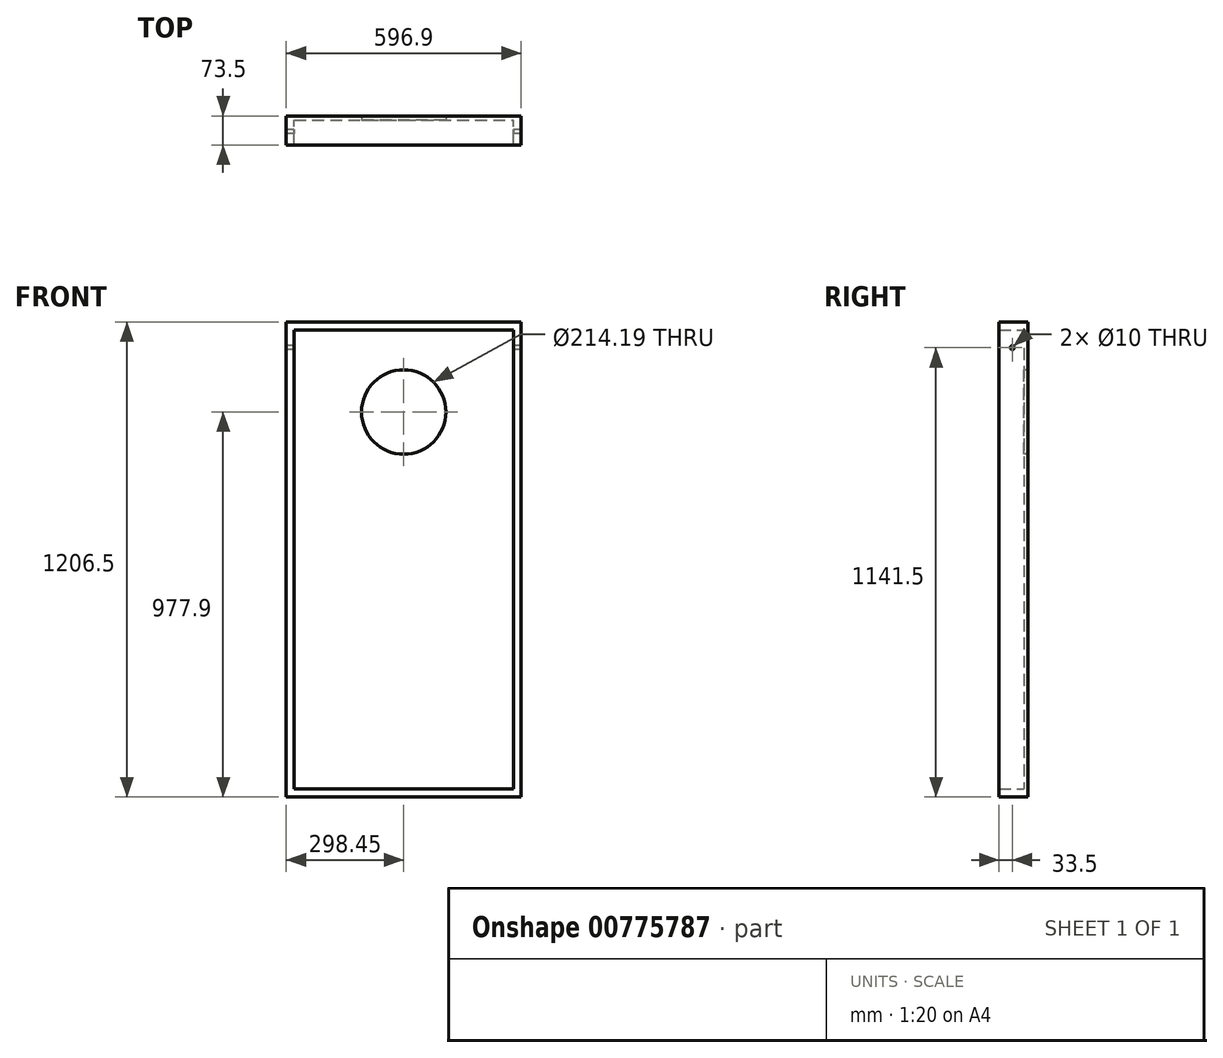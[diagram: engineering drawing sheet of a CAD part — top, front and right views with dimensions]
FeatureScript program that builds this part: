
annotation { "Feature Type Name" : "Feature", "Feature Type Description" : "" }
export const myFeature = defineFeature(function(context is Context, id is Id, definition is map)
    precondition{}
    {
        {
            var Q0;
            Q0=qCreatedBy(makeId("Front.planeOp"),FACE);
            var sketch = newSketch(context, id + "F0", { "sketchPlane" : qUnion([Q0])});
            skLineSegment(sketch, "E0.bottom", {"start": v(0, 0) * mm, "end": v(596.9, 0) * mm});
            skLineSegment(sketch, "E0.top", {"start": v(0, -1206.5) * mm, "end": v(596.9, -1206.5) * mm});
            skLineSegment(sketch, "E0.left", {"start": v(0, 0) * mm, "end": v(0, -1206.5) * mm});
            skLineSegment(sketch, "E0.right", {"start": v(596.9, 0) * mm, "end": v(596.9, -1206.5) * mm});
            skLineSegment(sketch, "E1.bottom", {"start": v(20, -20) * mm, "end": v(576.9, -20) * mm});
            skLineSegment(sketch, "E1.top", {"start": v(20, -1186.5) * mm, "end": v(576.9, -1186.5) * mm});
            skLineSegment(sketch, "E1.left", {"start": v(20, -20) * mm, "end": v(20, -1186.5) * mm});
            skLineSegment(sketch, "E1.right", {"start": v(576.9, -20) * mm, "end": v(576.9, -1186.5) * mm});
            skSolve(sketch);
        }
        {
            var Q0;
            Q0 = qSketchRegion(id + "F0", true);
            extrude(context, id + "F1", {"entities" : qUnion([Q0]), "depth" : (2.5 * 25.4) * mm, "offsetDistance" : 25 * mm});
        }
        {
            var Q0;
            Q0=qCreatedBy(makeId("Front.planeOp"),FACE);
            var sketch = newSketch(context, id + "F2", { "sketchPlane" : qUnion([Q0])});
            skLineSegment(sketch, "E2.bottom", {"start": v(0, 0) * mm, "end": v(596.9, 0) * mm});
            skLineSegment(sketch, "E2.top", {"start": v(0, -1206.5) * mm, "end": v(596.9, -1206.5) * mm});
            skLineSegment(sketch, "E2.left", {"start": v(0, 0) * mm, "end": v(0, -1206.5) * mm});
            skLineSegment(sketch, "E2.right", {"start": v(596.9, 0) * mm, "end": v(596.9, -1206.5) * mm});
            skCircle(sketch, "E3", {"center": v(298.45, -228.6) * mm, "radius": 107.1 * mm});
            skSolve(sketch);
        }
        {
            var Q0;
            Q0 = qSketchRegion(id + "F2", true);
            extrude(context, id + "F3", {"entities" : qUnion([Q0]), "operationType" : NewBodyOperationType.ADD, "oppositeDirection" : true, "depth" : 10 * mm, "offsetDistance" : 25 * mm});
        }
        {
            var Q0;
            Q0=qCreatedBy(makeId("Right.planeOp"),FACE);
            var sketch = newSketch(context, id + "F4", { "sketchPlane" : qUnion([Q0])});
            skCircle(sketch, "E4", {"center": v(-30, -65) * mm, "radius": 5 * mm});
            skSolve(sketch);
        }
        {
            var Q0;
            Q0=makeQuery(id+"F4.imprint","IMPRINT",FACE,{"disambiguationData":[TD([[makeQuery(id+"F4.imprint","IMPRINT",EDGE,{"derivedFrom":sQuery(id+"F4.wireOp",EDGE,"E4")}),1.0]])]});
            var Q1;
            Q1=makeQuery(id+"F3.boolean.opBoolean","MERGE",FACE,{"derivedFrom":[makeQuery(id+"F1.opExtrude","SWEPT_FACE",FACE,{"disambiguationData":[OSD([sQuery(id+"F0.wireOp",EDGE,"E0.right")])]}),makeQuery(id+"F3.opExtrude","SWEPT_FACE",FACE,{"disambiguationData":[OSD([sQuery(id+"F2.wireOp",EDGE,"E2.right")])]})]});
            extrude(context, id + "F5", {"entities" : qUnion([Q0]), "operationType" : NewBodyOperationType.REMOVE, "endBound" : BoundingType.UP_TO_SURFACE, "depth" : 25 * mm, "endBoundEntityFace" : qUnion([Q1]), "offsetDistance" : 25 * mm});
        }
    });
